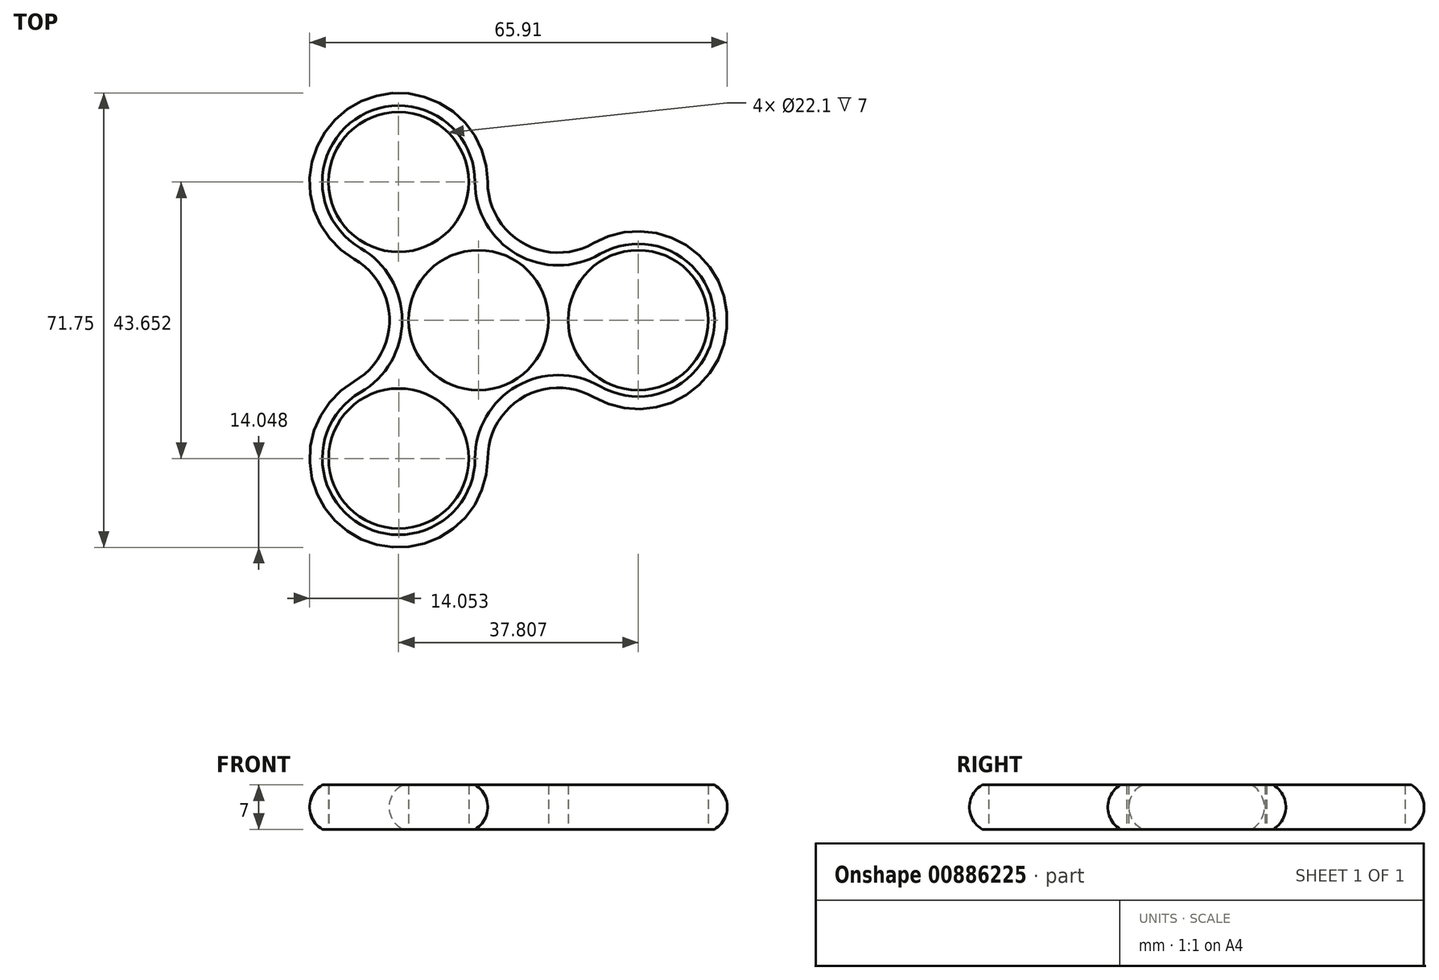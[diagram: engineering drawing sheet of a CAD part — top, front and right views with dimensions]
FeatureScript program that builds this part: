
annotation { "Feature Type Name" : "Feature", "Feature Type Description" : "" }
export const myFeature = defineFeature(function(context is Context, id is Id, definition is map)
    precondition{}
    {
        {
            var Q0;
            Q0=qCreatedBy(makeId("Top.planeOp"),FACE);
            var sketch = newSketch(context, id + "F0", { "sketchPlane" : qUnion([Q0])});
            skCircle(sketch, "E0", {"center": v(0, 0) * mm, "radius": 11.05 * mm});
            skLineSegment(sketch, "E1", {"start": v(0, 0) * mm, "end": v(25.2, 0) * mm, "construction": true});
            skCircle(sketch, "E2", {"center": v(25.2, 0) * mm, "radius": 11.05 * mm});
            skCircle(sketch, "E3", {"center": v(0, 0) * mm, "radius": 25.2 * mm, "construction": true});
            skCircle(sketch, "E4.0", {"center": v(25.2, 0) * mm, "radius": 12.05 * mm});
            skCircle(sketch, "E5.1.0", {"center": v(-12.6, 21.82) * mm, "radius": 12.05 * mm});
            skCircle(sketch, "E5.1.1", {"center": v(-12.6, 21.82) * mm, "radius": 11.05 * mm});
            skCircle(sketch, "E5.2.0", {"center": v(-12.6, -21.83) * mm, "radius": 12.05 * mm});
            skCircle(sketch, "E5.2.1", {"center": v(-12.6, -21.83) * mm, "radius": 11.05 * mm});
            skLineSegment(sketch, "E6", {"start": v(-12.6, 21.82) * mm, "end": v(12.6, -21.82) * mm, "construction": true});
            skLineSegment(sketch, "E7", {"start": v(-12.6, -21.83) * mm, "end": v(12.6, -21.82) * mm, "construction": true});
            skLineSegment(sketch, "E8", {"start": v(12.6, -21.82) * mm, "end": v(25.2, 0) * mm, "construction": true});
            skLineSegment(sketch, "E9", {"start": v(5.52, -9.57) * mm, "end": v(6.02, -10.44) * mm, "construction": true});
            skArc(sketch, "E10", {"start": v(19.17, -10.44) * mm, "mid": v(6.02, -10.44) * mm, "end": v(-0.55, -21.83) * mm});
            skArc(sketch, "E11.1.0", {"start": v(-0.56, 21.82) * mm, "mid": v(6.02, 10.43) * mm, "end": v(19.17, 10.43) * mm});
            skArc(sketch, "E11.2.0", {"start": v(-18.62, -11.4) * mm, "mid": v(-12.05, 0) * mm, "end": v(-18.63, 11.38) * mm});
            skSolve(sketch);
        }
        {
            var Q0;
            Q0=makeQuery(id+"F0.imprint","IMPRINT",FACE,{"disambiguationData":[TD([[makeQuery(id+"F0.imprint","IMPRINT",EDGE,{"derivedFrom":sQuery(id+"F0.wireOp",EDGE,"E0")}),-1.0]])]});
            var Q1;
            Q1=makeQuery(id+"F0.imprint","IMPRINT",FACE,{"disambiguationData":[TD([[makeQuery(id+"F0.imprint","IMPRINT",EDGE,{"derivedFrom":sQuery(id+"F0.wireOp",EDGE,"E5.1.1")}),-1.0]])]});
            var Q2;
            Q2=makeQuery(id+"F0.imprint","IMPRINT",FACE,{"disambiguationData":[TD([[makeQuery(id+"F0.imprint","IMPRINT",EDGE,{"derivedFrom":sQuery(id+"F0.wireOp",EDGE,"E2")}),-1.0]])]});
            var Q3;
            Q3=makeQuery(id+"F0.imprint","IMPRINT",FACE,{"disambiguationData":[TD([[makeQuery(id+"F0.imprint","IMPRINT",EDGE,{"derivedFrom":sQuery(id+"F0.wireOp",EDGE,"E5.2.1")}),-1.0]])]});
            extrude(context, id + "F1", {"entities" : qUnion([Q0, Q1, Q2, Q3]), "depth" : 7 * mm, "offsetDistance" : 25 * mm});
        }
        {
            var Q0;
            Q0=qCreatedBy(makeId("Front.planeOp"),FACE);
            var sketch = newSketch(context, id + "F2", { "sketchPlane" : qUnion([Q0])});
            skPoint(sketch, "E12.0", {"position": v(37.25, 7) * mm});
            skPoint(sketch, "E13.0", {"position": v(37.25, 0) * mm});
            skArc(sketch, "E14", {"start": v(37.25, 0) * mm, "mid": v(39.25, 3.5) * mm, "end": v(37.25, 7) * mm});
            skLineSegment(sketch, "E15", {"start": v(37.25, 7) * mm, "end": v(37.25, 0) * mm});
            skPoint(sketch, "E16", {"position": v(37.25, 3.5) * mm});
            skPoint(sketch, "E17", {"position": v(39.25, 3.5) * mm});
            skSolve(sketch);
        }
        {
            var Q0;
            Q0=makeQuery(id+"F2.imprint","IMPRINT",FACE,{"disambiguationData":[TD([[makeQuery(id+"F2.imprint","IMPRINT",EDGE,{"derivedFrom":sQuery(id+"F2.wireOp",EDGE,"s32fWGcO-ubQ4-Y1d4-2bjF-cBnH2Gjxc5p4")}),1.0]])]});
            var Q1;
            Q1=makeQuery(id+"F2.imprint","IMPRINT",FACE,{"disambiguationData":[TD([[makeQuery(id+"F2.imprint","IMPRINT",EDGE,{"derivedFrom":sQuery(id+"F2.wireOp",EDGE,"E14")}),1.0]])]});
            var Q2;
            Q2=makeQuery(id+"F1.opExtrude","CAP_EDGE",EDGE,{"disambiguationData":[OSD([sQuery(id+"F0.wireOp",EDGE,"E4.0")])],"isStart":false});
            var Q3;
            Q3=makeQuery(id+"F1.opExtrude","CAP_EDGE",EDGE,{"disambiguationData":[OSD([sQuery(id+"F0.wireOp",EDGE,"E10")])],"isStart":false});
            var Q4;
            Q4=makeQuery(id+"F1.opExtrude","CAP_EDGE",EDGE,{"disambiguationData":[OSD([sQuery(id+"F0.wireOp",EDGE,"E5.2.0")])],"isStart":false});
            var Q5;
            Q5=makeQuery(id+"F1.opExtrude","CAP_EDGE",EDGE,{"disambiguationData":[OSD([sQuery(id+"F0.wireOp",EDGE,"E5.1.0")])],"isStart":false});
            var Q6;
            Q6=makeQuery(id+"F1.opExtrude","CAP_EDGE",EDGE,{"disambiguationData":[OSD([sQuery(id+"F0.wireOp",EDGE,"E11.2.0")])],"isStart":false});
            var Q7;
            Q7=makeQuery(id+"F1.opExtrude","CAP_EDGE",EDGE,{"disambiguationData":[OSD([sQuery(id+"F0.wireOp",EDGE,"E11.1.0")])],"isStart":false});
            sweep(context, id + "F3", {"operationType" : NewBodyOperationType.ADD, "profiles" : qUnion([Q0, Q1]), "path" : qUnion([Q2, Q3, Q4, Q5, Q6, Q7])});
        }
    });
